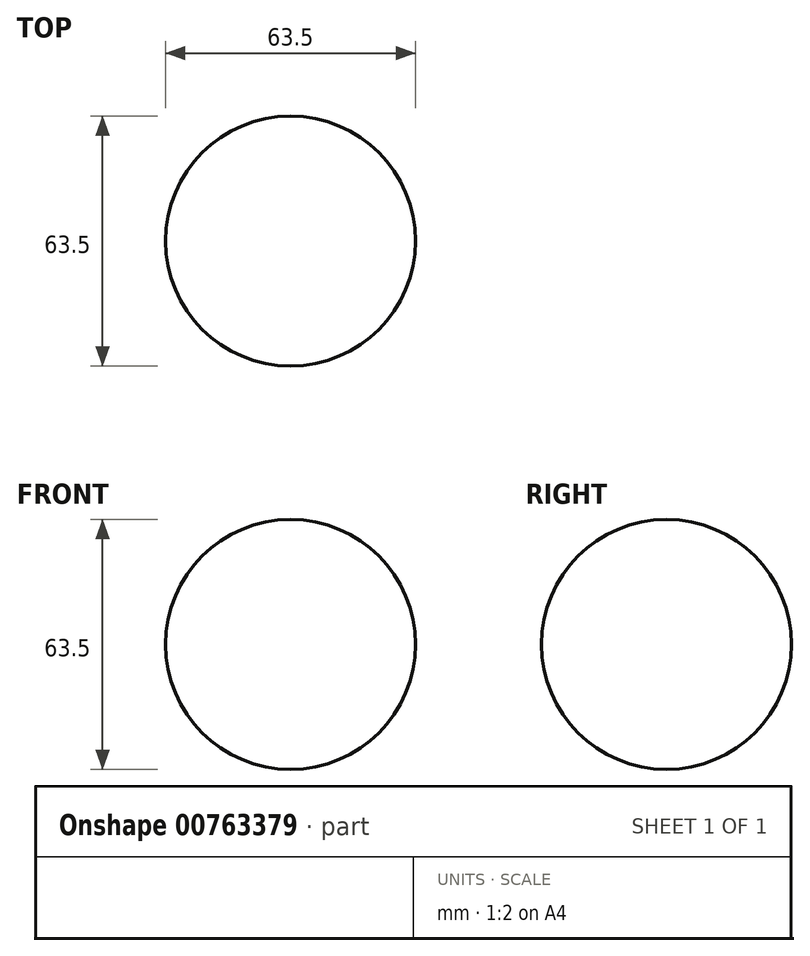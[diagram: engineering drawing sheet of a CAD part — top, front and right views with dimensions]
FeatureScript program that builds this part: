
annotation { "Feature Type Name" : "Feature", "Feature Type Description" : "" }
export const myFeature = defineFeature(function(context is Context, id is Id, definition is map)
    precondition{}
    {
        {
            var Q0;
            Q0=qCreatedBy(makeId("Front.planeOp"),FACE);
            var sketch = newSketch(context, id + "F0", { "sketchPlane" : qUnion([Q0])});
            skCircle(sketch, "E0", {"center": v(0, 0) * mm, "radius": 31.75 * mm});
            skLineSegment(sketch, "E1", {"start": v(0, 31.75) * mm, "end": v(0, -31.75) * mm});
            skSolve(sketch);
        }
        {
            var Q0;
            {var subQ0=sQuery(id+"F0.wireOp",EDGE,"E1");Q0=makeQuery(id+"F0.imprint","IMPRINT",FACE,{"disambiguationData":[TD([[makeQuery(id+"F0.imprint","IMPRINT",EDGE,{"derivedFrom":subQ0}),-1.0]])]});}
            var Q1;
            Q1=sQuery(id+"F0.wireOp",EDGE,"E1");
            revolve(context, id + "F1", {"surfaceOperationType" : NewSurfaceOperationType.NEW, "entities" : qUnion([Q0]), "axis" : qUnion([Q1]), "revolveType" : RevolveType.FULL});
        }
    });
